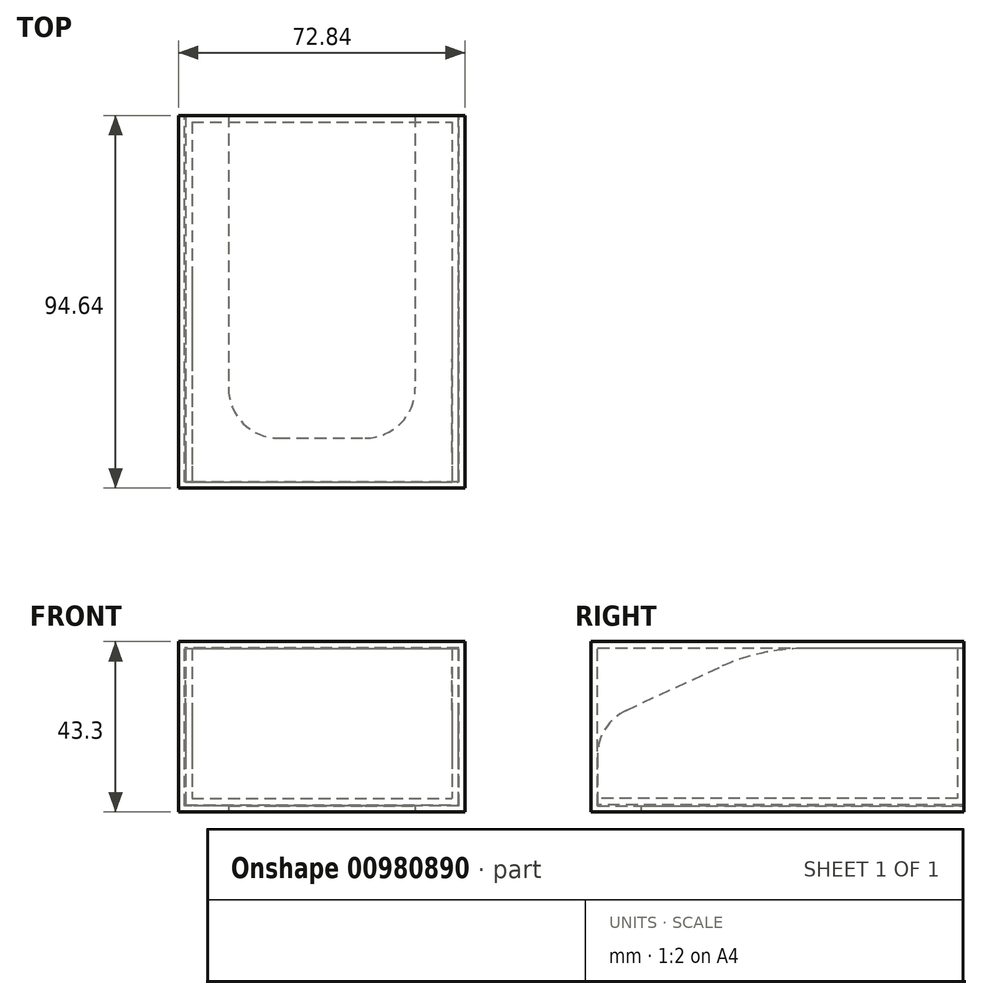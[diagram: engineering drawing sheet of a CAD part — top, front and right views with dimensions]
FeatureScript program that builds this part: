
annotation { "Feature Type Name" : "Feature", "Feature Type Description" : "" }
export const myFeature = defineFeature(function(context is Context, id is Id, definition is map)
    precondition{}
    {
        {
            var Q0;
            Q0=qCreatedBy(makeId("Top.planeOp"),FACE);
            var sketch = newSketch(context, id + "F0", { "sketchPlane" : qUnion([Q0])});
            skLineSegment(sketch, "E0.bottom", {"start": v(-33.02, 45.72) * mm, "end": v(33.02, 45.72) * mm});
            skLineSegment(sketch, "E0.top", {"start": v(-33.02, -45.72) * mm, "end": v(33.02, -45.72) * mm});
            skLineSegment(sketch, "E0.left", {"start": v(-33.02, 45.72) * mm, "end": v(-33.02, -45.72) * mm});
            skLineSegment(sketch, "E0.right", {"start": v(33.02, 45.72) * mm, "end": v(33.02, -45.72) * mm});
            skSolve(sketch);
        }
        {
            var Q0;
            Q0 = qSketchRegion(id + "F0", true);
            extrude(context, id + "F1", {"entities" : qUnion([Q0]), "depth" : 38.1 * mm, "offsetDistance" : 25.4 * mm});
        }
        {
            var Q0;
            Q0=makeQuery(id+"F1.opExtrude","CAP_FACE",FACE,{"disambiguationData":[OSD([sQuery(id+"F0.wireOp",EDGE,"E0.bottom"),sQuery(id+"F0.wireOp",EDGE,"E0.top"),sQuery(id+"F0.wireOp",EDGE,"E0.left"),sQuery(id+"F0.wireOp",EDGE,"E0.right")])],"isStart":false});
            var Q1;
            Q1=makeQuery(id+"F1.opExtrude","SWEPT_FACE",FACE,{"disambiguationData":[OSD([sQuery(id+"F0.wireOp",EDGE,"E0.top")])]});
            shell(context, id + "F2", {"entities" : qUnion([Q0, Q1]), "thickness" : 1.6 * mm, "oppositeDirection" : true});
        }
        {
            var Q0;
            {var subQ0=sQuery(id+"F0.wireOp",EDGE,"E0.top");Q0=makeQuery(id+"F2.opShell","OFFSET_EDGE",EDGE,{"disambiguationData":[OSD([subQ0]),TDD([makeQuery(id+"F1.opExtrude","CAP_EDGE",EDGE,{"disambiguationData":[OSD([subQ0])],"isStart":false})])]});}
            var Q1;
            Q1=makeQuery(id+"F1.opExtrude","CAP_EDGE",EDGE,{"disambiguationData":[OSD([sQuery(id+"F0.wireOp",EDGE,"E0.top")])],"isStart":false});
            chamfer(context, id + "F3", {"entities" : qUnion([Q0, Q1]), "chamferType" : ChamferType.TWO_OFFSETS, "width1" : 41.27 * mm, "oppositeDirection" : false, "width2" : 19.05 * mm, "tangentPropagation" : true});
        }
        {
            var Q0;
            {var subQ0=sQuery(id+"F0.wireOp",EDGE,"E0.top");Q0=makeQuery(id+"F3.opChamfer","BLEND_EDGE",EDGE,{"blendedFrom":[makeQuery(id+"F1.opExtrude","CAP_EDGE",EDGE,{"disambiguationData":[OSD([subQ0])],"isStart":false}),makeQuery(id+"F1.opExtrude","CAP_FACE",FACE,{"disambiguationData":[OSD([sQuery(id+"F0.wireOp",EDGE,"E0.bottom"),subQ0,sQuery(id+"F0.wireOp",EDGE,"E0.left"),sQuery(id+"F0.wireOp",EDGE,"E0.right")])],"isStart":false})],"blendedInto":[makeQuery(id+"F1.opExtrude","CAP_FACE",FACE,{"disambiguationData":[OSD([sQuery(id+"F0.wireOp",EDGE,"E0.bottom"),subQ0,sQuery(id+"F0.wireOp",EDGE,"E0.left"),sQuery(id+"F0.wireOp",EDGE,"E0.right")])],"isStart":false})]});}
            var Q1;
            {var subQ0=sQuery(id+"F0.wireOp",EDGE,"E0.top");Q1=makeQuery(id+"F3.opChamfer","BLEND_EDGE",EDGE,{"blendedFrom":[makeQuery(id+"F2.opShell","OFFSET_EDGE",EDGE,{"disambiguationData":[OSD([subQ0]),TDD([makeQuery(id+"F1.opExtrude","CAP_EDGE",EDGE,{"disambiguationData":[OSD([subQ0])],"isStart":false})])]}),makeQuery(id+"F1.opExtrude","CAP_FACE",FACE,{"disambiguationData":[OSD([sQuery(id+"F0.wireOp",EDGE,"E0.bottom"),subQ0,sQuery(id+"F0.wireOp",EDGE,"E0.left"),sQuery(id+"F0.wireOp",EDGE,"E0.right")])],"isStart":false})],"blendedInto":[makeQuery(id+"F1.opExtrude","CAP_FACE",FACE,{"disambiguationData":[OSD([sQuery(id+"F0.wireOp",EDGE,"E0.bottom"),subQ0,sQuery(id+"F0.wireOp",EDGE,"E0.left"),sQuery(id+"F0.wireOp",EDGE,"E0.right")])],"isStart":false})]});}
            fillet(context, id + "F4", {"entities" : qUnion([Q0, Q1]), "radius" : 50.8 * mm, "tangentPropagation" : true, "allowEdgeOverflow" : false});
        }
        {
            var Q0;
            {var subQ0=sQuery(id+"F0.wireOp",EDGE,"E0.top");Q0=makeQuery(id+"F3.opChamfer","BLEND_EDGE",EDGE,{"blendedFrom":[makeQuery(id+"F1.opExtrude","CAP_EDGE",EDGE,{"disambiguationData":[OSD([subQ0])],"isStart":false}),makeQuery(id+"F1.opExtrude","SWEPT_FACE",FACE,{"disambiguationData":[OSD([subQ0])]})],"blendedInto":[makeQuery(id+"F1.opExtrude","SWEPT_FACE",FACE,{"disambiguationData":[OSD([subQ0])]})]});}
            var Q1;
            {var subQ0=sQuery(id+"F0.wireOp",EDGE,"E0.top");Q1=makeQuery(id+"F3.opChamfer","BLEND_EDGE",EDGE,{"blendedFrom":[makeQuery(id+"F2.opShell","OFFSET_EDGE",EDGE,{"disambiguationData":[OSD([subQ0]),TDD([makeQuery(id+"F1.opExtrude","CAP_EDGE",EDGE,{"disambiguationData":[OSD([subQ0])],"isStart":false})])]}),makeQuery(id+"F1.opExtrude","SWEPT_FACE",FACE,{"disambiguationData":[OSD([subQ0])]})],"blendedInto":[makeQuery(id+"F1.opExtrude","SWEPT_FACE",FACE,{"disambiguationData":[OSD([subQ0])]})]});}
            fillet(context, id + "F5", {"entities" : qUnion([Q0, Q1]), "radius" : 12.7 * mm, "tangentPropagation" : true, "allowEdgeOverflow" : false});
        }
        {
            var Q0;
            Q0=qCreatedBy(makeId("Front.planeOp"),FACE);
            var sketch = newSketch(context, id + "F6", { "sketchPlane" : qUnion([Q0])});
            skLineSegment(sketch, "E1.bottom", {"start": v(-34.82, 38.3) * mm, "end": v(34.82, 38.3) * mm});
            skLineSegment(sketch, "E1.top", {"start": v(-34.82, -1.8) * mm, "end": v(34.82, -1.8) * mm});
            skLineSegment(sketch, "E1.left", {"start": v(-34.82, 38.3) * mm, "end": v(-34.82, -1.8) * mm});
            skLineSegment(sketch, "E1.right", {"start": v(34.82, 38.3) * mm, "end": v(34.82, -1.8) * mm});
            skSolve(sketch);
        }
        {
            var Q0;
            Q0=makeQuery(id+"F6.imprint","IMPRINT",FACE,{"disambiguationData":[TD([[makeQuery(id+"F6.imprint","IMPRINT",EDGE,{"derivedFrom":sQuery(id+"F6.wireOp",EDGE,"E1.bottom")}),-1.0]])]});
            var Q1;
            Q1=makeQuery(id+"F1.opExtrude","SWEPT_FACE",FACE,{"disambiguationData":[OSD([sQuery(id+"F0.wireOp",EDGE,"E0.top")])]});
            var Q2;
            Q2=makeQuery(id+"F1.opExtrude","SWEPT_FACE",FACE,{"disambiguationData":[OSD([sQuery(id+"F0.wireOp",EDGE,"E0.bottom")])]});
            extrude(context, id + "F7", {"entities" : qUnion([Q0]), "endBound" : BoundingType.UP_TO_SURFACE, "depth" : 25.4 * mm, "endBoundEntityFace" : qUnion([Q1]), "offsetDistance" : 25.4 * mm, "hasSecondDirection" : true, "secondDirectionBound" : SecondDirectionBoundingType.UP_TO_SURFACE, "secondDirectionOppositeDirection" : true, "secondDirectionDepth" : 25.4 * mm, "secondDirectionBoundEntityFace" : qUnion([Q2])});
        }
        {
            var Q0;
            Q0=makeQuery(id+"F7.opExtrude","CAP_FACE",FACE,{"disambiguationData":[OSD([sQuery(id+"F6.wireOp",EDGE,"E1.bottom"),sQuery(id+"F6.wireOp",EDGE,"E1.top"),sQuery(id+"F6.wireOp",EDGE,"E1.left"),sQuery(id+"F6.wireOp",EDGE,"E1.right")])],"isStart":true});
            shell(context, id + "F8", {"entities" : qUnion([Q0]), "thickness" : 1.6 * mm, "oppositeDirection" : true});
        }
        {
            var Q0;
            Q0=makeQuery(id+"F7.opExtrude","SWEPT_FACE",FACE,{"disambiguationData":[OSD([sQuery(id+"F6.wireOp",EDGE,"E1.top")])]});
            var sketch = newSketch(context, id + "F9", { "sketchPlane" : qUnion([Q0])});
            skLineSegment(sketch, "E2.bottom", {"start": v(-23.72, -47.32) * mm, "end": v(23.72, -47.32) * mm});
            skLineSegment(sketch, "E2.top", {"start": v(-11.02, 34.62) * mm, "end": v(11.02, 34.62) * mm});
            skLineSegment(sketch, "E2.left", {"start": v(-23.72, -47.32) * mm, "end": v(-23.72, 21.92) * mm});
            skLineSegment(sketch, "E2.right", {"start": v(23.72, -47.32) * mm, "end": v(23.72, 21.92) * mm});
            skPoint(sketch, "E3.visualSharp", {"position": v(-23.72, 34.62) * mm});
            skArc(sketch, "E3.filletArc", {"start": v(-11.02, 34.62) * mm, "mid": v(-20, 30.9) * mm, "end": v(-23.72, 21.92) * mm});
            skPoint(sketch, "E4.visualSharp", {"position": v(23.72, 34.62) * mm});
            skArc(sketch, "E4.filletArc", {"start": v(23.72, 21.92) * mm, "mid": v(20, 30.9) * mm, "end": v(11.02, 34.62) * mm});
            skSolve(sketch);
        }
        {
            var Q0;
            Q0=makeQuery(id+"F9.imprint","IMPRINT",FACE,{"disambiguationData":[TD([[makeQuery(id+"F9.imprint","IMPRINT",EDGE,{"derivedFrom":sQuery(id+"F9.wireOp",EDGE,"E2.bottom")}),-1.0]])]});
            extrude(context, id + "F10", {"entities" : qUnion([Q0]), "operationType" : NewBodyOperationType.REMOVE, "endBound" : BoundingType.UP_TO_NEXT, "oppositeDirection" : true, "depth" : 25.4 * mm, "offsetDistance" : 25.4 * mm});
        }
    });
